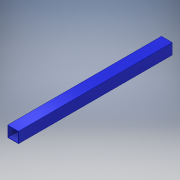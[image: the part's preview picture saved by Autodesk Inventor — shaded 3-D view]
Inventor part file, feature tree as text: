
AUTODESK INVENTOR PART (.ipt)
format: ipt  version: 2017 (Build 210142000, 142)  size: 101,888 bytes
history: native  units: in
note: dims shown in document units (in); Inventor stores cm internally (conversion verified against a paired STEP export)
features: extrude x1, sketch x1
ambient origin geometry x8: Origin, YZ Plane, XZ Plane, XY Plane, X Axis, Y Axis, Z Axis, Center Point
bodies: Solid1 (feature_tree)
feature tree (2):
  extrude  "Extrusion1"  Depth=3.937in
  sketch  "Sketch1"  dims[d0=3.937in d1=3.937in d2=0.1969in d3=0.1969in d4=0.1969in d5=0.1969in d6=55.9055in d7=0.0in]
